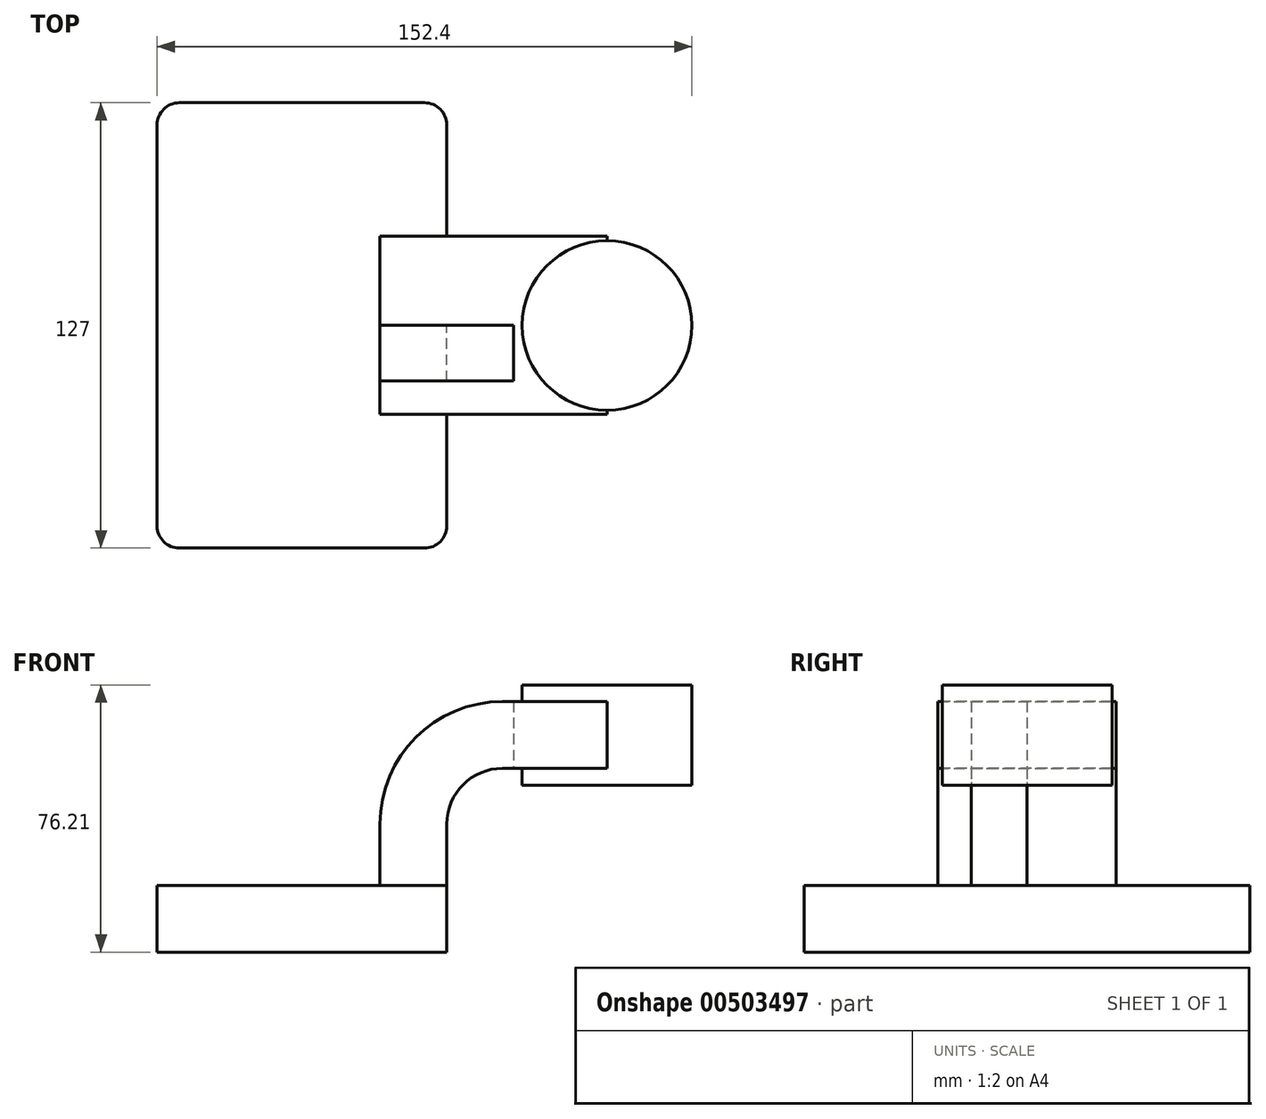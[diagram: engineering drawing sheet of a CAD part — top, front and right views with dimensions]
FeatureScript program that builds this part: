
annotation { "Feature Type Name" : "Feature", "Feature Type Description" : "" }
export const myFeature = defineFeature(function(context is Context, id is Id, definition is map)
    precondition{}
    {
        {
            var Q0;
            Q0=qCreatedBy(makeId("Front.planeOp"),FACE);
            var sketch = newSketch(context, id + "F0", { "sketchPlane" : qUnion([Q0])});
            skLineSegment(sketch, "E0.bottom", {"start": v(41.28, 9.53) * mm, "end": v(-41.28, 9.53) * mm});
            skLineSegment(sketch, "E0.top", {"start": v(41.28, -9.53) * mm, "end": v(-41.28, -9.53) * mm});
            skLineSegment(sketch, "E0.left", {"start": v(41.28, 9.53) * mm, "end": v(41.28, -9.53) * mm});
            skLineSegment(sketch, "E0.right", {"start": v(-41.28, 9.53) * mm, "end": v(-41.28, -9.53) * mm});
            skPoint(sketch, "E0.middle", {"position": v(0, 0) * mm});
            skLineSegment(sketch, "E1.bottom", {"start": v(111.13, 66.68) * mm, "end": v(60.33, 66.68) * mm});
            skLineSegment(sketch, "E1.top", {"start": v(111.13, 38.1) * mm, "end": v(60.33, 38.1) * mm});
            skLineSegment(sketch, "E1.left", {"start": v(111.13, 66.68) * mm, "end": v(111.13, 38.1) * mm});
            skLineSegment(sketch, "E1.right", {"start": v(60.33, 66.68) * mm, "end": v(60.33, 38.1) * mm});
            skPoint(sketch, "E1.middle", {"position": v(85.72, 52.39) * mm});
            skLineSegment(sketch, "E2", {"start": v(41.27, 9.53) * mm, "end": v(41.27, 27) * mm});
            skArc(sketch, "E3", {"start": v(41.27, 27) * mm, "mid": v(45.92, 38.23) * mm, "end": v(57.15, 42.88) * mm});
            skLineSegment(sketch, "E4", {"start": v(57.15, 42.88) * mm, "end": v(86.95, 42.88) * mm});
            skLineSegment(sketch, "E5.0", {"start": v(57.15, 61.93) * mm, "end": v(86.95, 61.93) * mm});
            skArc(sketch, "E5.1", {"start": v(22.23, 27) * mm, "mid": v(32.45, 51.7) * mm, "end": v(57.15, 61.93) * mm});
            skLineSegment(sketch, "E5.2", {"start": v(22.22, 9.26) * mm, "end": v(22.22, 27) * mm});
            skLineSegment(sketch, "E6", {"start": v(86.95, 42.88) * mm, "end": v(86.95, 66.68) * mm});
            skFitSpline(sketch, "E7", {"points": [v(-41.28, 9.53) * mm, v(57.15, 61.93) * mm], "startDerivative": vector(3.18, 84) * mm, "endDerivative": vector(118.3, -9.4) * mm});
            skLineSegment(sketch, "E8", {"start": v(86.95, 66.68) * mm, "end": v(86.95, 38.1) * mm});
            skSolve(sketch);
        }
        {
            var Q0;
            Q0=makeQuery(id+"F0.imprint","IMPRINT",FACE,{"disambiguationData":[TD([[makeQuery(id+"F0.imprint","IMPRINT",EDGE,{"derivedFrom":sQuery(id+"F0.wireOp",EDGE,"E0.top")}),-1.0]])]});
            extrude(context, id + "F1", {"entities" : qUnion([Q0]), "endBound" : BoundingType.SYMMETRIC, "depth" : 127 * mm});
        }
        {
            var Q0;
            {var subQ1=sQuery(id+"F0.wireOp",EDGE,"E2");Q0=makeQuery(id+"F0.imprint","IMPRINT",FACE,{"disambiguationData":[TD([[makeQuery(id+"F0.imprint","IMPRINT",EDGE,{"derivedFrom":subQ1}),1.0]])]});}
            var Q1;
            {var subQ0=sQuery(id+"F0.wireOp",EDGE,"E5.0");var subQ1=sQuery(id+"F0.wireOp",EDGE,"E1.right");var subQ2=makeQuery(id+"F0.imprint","INTERSECT",VERTEX,{"derivedFrom":[subQ1,subQ0]});Q1=makeQuery(id+"F0.imprint","IMPRINT",FACE,{"disambiguationData":[TD([[makeQuery(id+"F0.imprint","IMPRINT",EDGE,{"disambiguationData":[TD([[subQ2,-1.0]])],"derivedFrom":subQ1}),1.0]])]});}
            var Q2;
            Q2=sQuery(id+"F0.wireOp",EDGE,"E4");
            var Q3;
            Q3=sQuery(id+"F0.wireOp",EDGE,"E6");
            var Q4;
            Q4=sQuery(id+"F0.wireOp",EDGE,"E5.0");
            var Q5;
            Q5=sQuery(id+"F0.wireOp",EDGE,"E5.1");
            var Q6;
            Q6=sQuery(id+"F0.wireOp",EDGE,"E3");
            extrude(context, id + "F2", {"entities" : qUnion([Q0, Q1]), "surfaceEntities" : qUnion([Q2, Q3, Q4, Q5, Q6]), "endBound" : BoundingType.SYMMETRIC, "depth" : 50.8 * mm});
        }
        {
            var Q0;
            {var subQ4=sQuery(id+"F0.wireOp",EDGE,"E5.1");Q0=makeQuery(id+"F0.imprint","IMPRINT",FACE,{"disambiguationData":[TD([[makeQuery(id+"F0.imprint","IMPRINT",EDGE,{"derivedFrom":subQ4}),1.0]])]});}
            extrude(context, id + "F3", {"entities" : qUnion([Q0]), "depth" : 15.88 * mm});
        }
        {
            var Q0;
            {var subQ0=sQuery(id+"F0.wireOp",EDGE,"E1.left");Q0=makeQuery(id+"F0.imprint","IMPRINT",FACE,{"disambiguationData":[TD([[makeQuery(id+"F0.imprint","IMPRINT",EDGE,{"derivedFrom":subQ0}),-1.0]])]});}
            var Q1;
            Q1=sQuery(id+"F0.wireOp",EDGE,"E8");
            revolve(context, id + "F4", {"operationType" : NewBodyOperationType.ADD, "entities" : qUnion([Q0]), "axis" : qUnion([Q1]), "revolveType" : RevolveType.FULL});
        }
        {
            var Q0;
            Q0=makeQuery(id+"F1.opExtrude","CAP_EDGE",EDGE,{"disambiguationData":[OSD([sQuery(id+"F0.wireOp",EDGE,"E0.left")])],"isStart":false});
            var Q1;
            Q1=makeQuery(id+"F1.opExtrude","CAP_EDGE",EDGE,{"disambiguationData":[OSD([sQuery(id+"F0.wireOp",EDGE,"E0.right")])],"isStart":false});
            var Q2;
            Q2=makeQuery(id+"F1.opExtrude","CAP_EDGE",EDGE,{"disambiguationData":[OSD([sQuery(id+"F0.wireOp",EDGE,"E0.right")])],"isStart":true});
            var Q3;
            Q3=makeQuery(id+"F1.opExtrude","CAP_EDGE",EDGE,{"disambiguationData":[OSD([sQuery(id+"F0.wireOp",EDGE,"E0.left")])],"isStart":true});
            fillet(context, id + "F5", {"entities" : qUnion([Q0, Q1, Q2, Q3]), "radius" : 6.35 * mm, "tangentPropagation" : true, "allowEdgeOverflow" : false});
        }
    });
